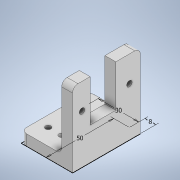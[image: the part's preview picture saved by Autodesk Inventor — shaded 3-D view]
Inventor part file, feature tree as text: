
AUTODESK INVENTOR PART (.ipt)
format: ipt  version: 2020.3 (Build 243373000, 373)  size: 304,128 bytes
history: native  units: mm
features: extrude x3, sketch x2, fillet x2
ambient origin geometry x8: Origin, YZ Plane, XZ Plane, XY Plane, X Axis, Y Axis, Z Axis, Center Point
bodies: Body1 (feature_tree)
feature tree (7):
  sketch  "Sketch1"  dims[d15=8.0mm d16=50.0mm]
  extrude  "Extrusion3"  Depth=50.0mm
  extrude  "Extrusion4"  Depth=8.0mm TaperAngle=0.0deg
  fillet  "Fillet1"  Radius=55.0mm
  extrude  "Extrusion5"  Depth=4.0mm
  fillet  "Fillet2"  Radius=10.0mm
  sketch  "Sketch2"  dims[d17=30.0mm d20=8.0mm d21=0.0mm d22=55.0mm d23=0.0mm d24=4.0mm d27=10.0mm d28=0.0mm d29=4.0mm d30=7.0mm d31=50.0mm d32=35.0mm d33=8.0mm d34=18.0mm d35=19.0mm d8=0.5mm d9=0.872665mm d10=0.5mm d11=0.872665mm]
